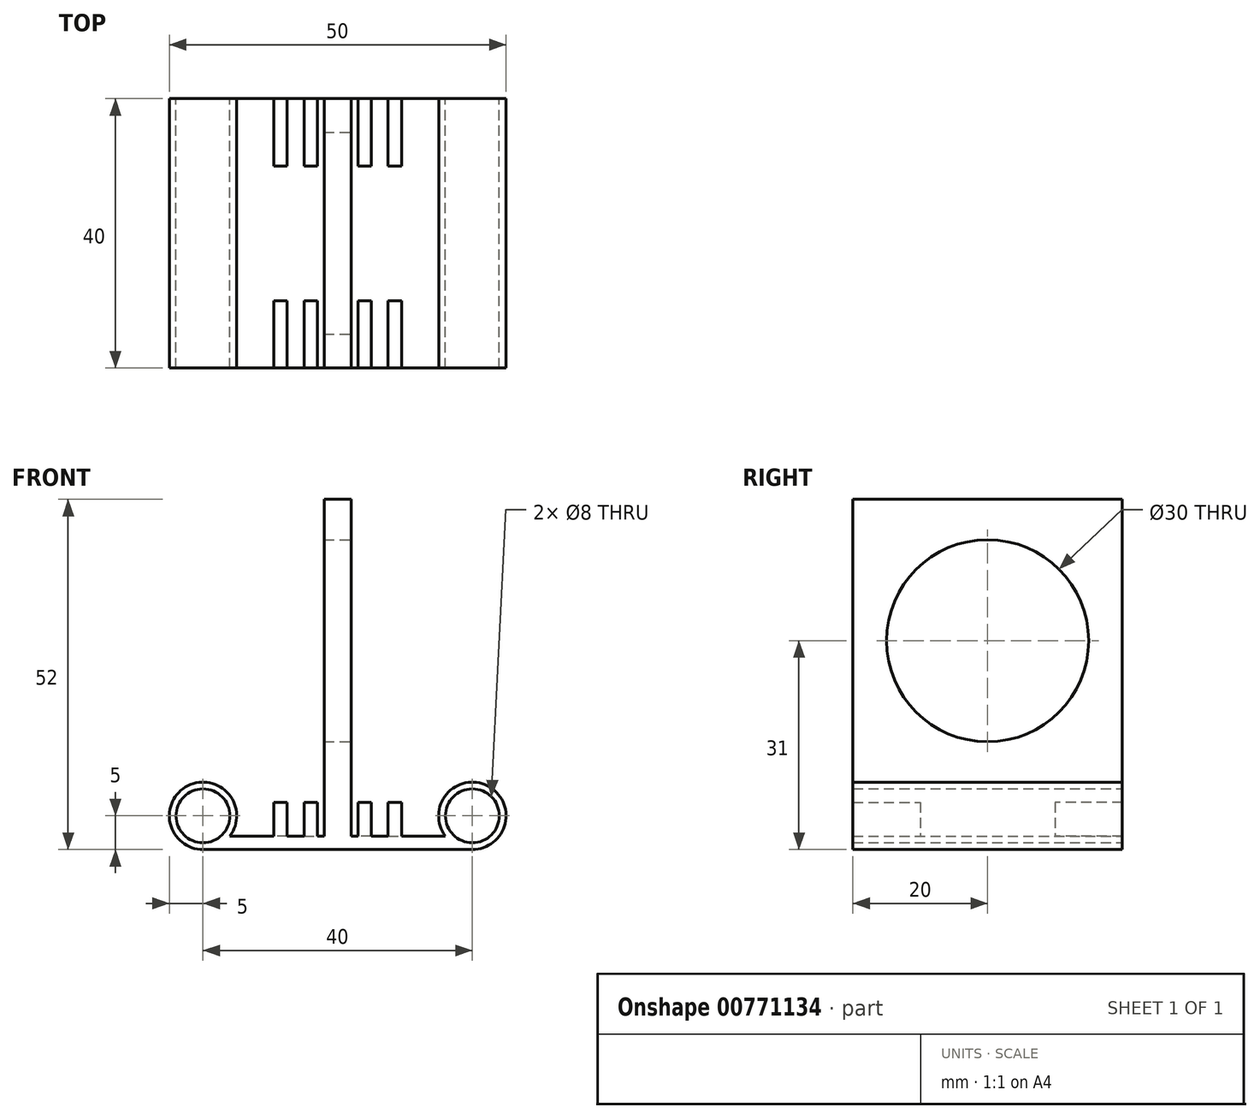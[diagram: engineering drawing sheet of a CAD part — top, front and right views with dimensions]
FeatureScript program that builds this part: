
annotation { "Feature Type Name" : "Feature", "Feature Type Description" : "" }
export const myFeature = defineFeature(function(context is Context, id is Id, definition is map)
    precondition{}
    {
        {
            var Q0;
            Q0=qCreatedBy(makeId("Front.planeOp"),FACE);
            var sketch = newSketch(context, id + "F0", { "sketchPlane" : qUnion([Q0])});
            skLineSegment(sketch, "E0.bottom", {"start": v(20, -1) * mm, "end": v(-20, -1) * mm});
            skLineSegment(sketch, "E0.top", {"start": v(16, 1) * mm, "end": v(-20, 1) * mm});
            skLineSegment(sketch, "E0.right", {"start": v(-20, -1) * mm, "end": v(-20, 1) * mm});
            skPoint(sketch, "E0.middle", {"position": v(0, 0) * mm});
            skArc(sketch, "E1", {"start": v(20, -1) * mm, "mid": v(22.24, 8.47) * mm, "end": v(16, 1) * mm});
            skPoint(sketch, "E1.second.point", {"position": v(20, 9) * mm});
            skPoint(sketch, "E1.third.point", {"position": v(24.89, 5.05) * mm});
            skCircle(sketch, "E2", {"center": v(20, 4) * mm, "radius": 4 * mm});
            skPoint(sketch, "E3.orphan", {"position": v(20, 1) * mm});
            skLineSegment(sketch, "E4.bottom", {"start": v(-2, 1) * mm, "end": v(2, 1) * mm});
            skLineSegment(sketch, "E4.top", {"start": v(-2, 51) * mm, "end": v(2, 51) * mm});
            skLineSegment(sketch, "E4.left", {"start": v(-2, 1) * mm, "end": v(-2, 51) * mm});
            skLineSegment(sketch, "E4.right", {"start": v(2, 1) * mm, "end": v(2, 51) * mm});
            skArc(sketch, "E5.MirrorCS", {"start": v(-20, -1) * mm, "mid": v(-22.24, 8.47) * mm, "end": v(-16, 1) * mm});
            skCircle(sketch, "E6.MirrorC", {"center": v(-20, 4) * mm, "radius": 4 * mm});
            skPoint(sketch, "E7.MirrorP", {"position": v(-20, 9) * mm});
            skPoint(sketch, "E8.MirrorP", {"position": v(-24.89, 5.05) * mm});
            skPoint(sketch, "E9.MirrorP", {"position": v(-20, 1) * mm});
            skSolve(sketch);
        }
        {
            var Q0;
            Q0 = qSketchRegion(id + "F0", true);
            extrude(context, id + "F1", {"entities" : qUnion([Q0]), "endBound" : BoundingType.SYMMETRIC, "depth" : 40 * mm, "offsetDistance" : 25 * mm});
        }
        {
            var Q0;
            {var subQ0=sQuery(id+"F0.wireOp",EDGE,"E0.top");Q0=makeQuery(id+"F1.opExtrude","SWEPT_FACE",FACE,{"disambiguationData":[OSD([subQ0]),TDD([makeQuery(id+"F0.imprint","IMPRINT",EDGE,{"disambiguationData":[TD([[makeQuery(id+"F0.imprint","INTERSECT",VERTEX,{"derivedFrom":[subQ0,sQuery(id+"F0.wireOp",EDGE,"E1")]}),-1.0]])],"derivedFrom":subQ0})])]});}
            var sketch = newSketch(context, id + "F2", { "sketchPlane" : qUnion([Q0])});
            skLineSegment(sketch, "E10.bottom", {"start": v(7.5, -20) * mm, "end": v(9.5, -20) * mm});
            skLineSegment(sketch, "E10.top", {"start": v(7.5, -10) * mm, "end": v(9.5, -10) * mm});
            skLineSegment(sketch, "E10.left", {"start": v(7.5, -20) * mm, "end": v(7.5, -10) * mm});
            skLineSegment(sketch, "E10.right", {"start": v(9.5, -20) * mm, "end": v(9.5, -10) * mm});
            skLineSegment(sketch, "E11.bottom", {"start": v(5, -20) * mm, "end": v(3, -20) * mm});
            skLineSegment(sketch, "E11.top", {"start": v(5, -10) * mm, "end": v(3, -10) * mm});
            skLineSegment(sketch, "E11.left", {"start": v(5, -20) * mm, "end": v(5, -10) * mm});
            skLineSegment(sketch, "E11.right", {"start": v(3, -20) * mm, "end": v(3, -10) * mm});
            skLineSegment(sketch, "E12.MirrorCS", {"start": v(-7.5, -20) * mm, "end": v(-7.5, -10) * mm});
            skLineSegment(sketch, "E13.MirrorCS", {"start": v(-5, -20) * mm, "end": v(-3, -20) * mm});
            skLineSegment(sketch, "E14.MirrorCS", {"start": v(-5, -20) * mm, "end": v(-5, -10) * mm});
            skLineSegment(sketch, "E15.MirrorCS", {"start": v(-3, -20) * mm, "end": v(-3, -10) * mm});
            skLineSegment(sketch, "E16.MirrorCS", {"start": v(-7.5, -20) * mm, "end": v(-9.5, -20) * mm});
            skLineSegment(sketch, "E17.MirrorCS", {"start": v(-9.5, -20) * mm, "end": v(-9.5, -10) * mm});
            skLineSegment(sketch, "E18.MirrorCS", {"start": v(-5, -10) * mm, "end": v(-3, -10) * mm});
            skLineSegment(sketch, "E19.MirrorCS", {"start": v(-7.5, -10) * mm, "end": v(-9.5, -10) * mm});
            skLineSegment(sketch, "E20.MirrorCS", {"start": v(7.5, 10) * mm, "end": v(9.5, 10) * mm});
            skLineSegment(sketch, "E21.MirrorCS", {"start": v(-7.5, 10) * mm, "end": v(-9.5, 10) * mm});
            skLineSegment(sketch, "E22.MirrorCS", {"start": v(7.5, 20) * mm, "end": v(9.5, 20) * mm});
            skLineSegment(sketch, "E23.MirrorCS", {"start": v(-5, 10) * mm, "end": v(-3, 10) * mm});
            skLineSegment(sketch, "E24.MirrorCS", {"start": v(5, 20) * mm, "end": v(3, 20) * mm});
            skLineSegment(sketch, "E25.MirrorCS", {"start": v(-7.5, 20) * mm, "end": v(-9.5, 20) * mm});
            skLineSegment(sketch, "E26.MirrorCS", {"start": v(-5, 20) * mm, "end": v(-3, 20) * mm});
            skLineSegment(sketch, "E27.MirrorCS", {"start": v(5, 10) * mm, "end": v(3, 10) * mm});
            skLineSegment(sketch, "E28.MirrorCS", {"start": v(-7.5, 20) * mm, "end": v(-7.5, 10) * mm});
            skLineSegment(sketch, "E29.MirrorCS", {"start": v(3, 20) * mm, "end": v(3, 10) * mm});
            skLineSegment(sketch, "E30.MirrorCS", {"start": v(-9.5, 20) * mm, "end": v(-9.5, 10) * mm});
            skLineSegment(sketch, "E31.MirrorCS", {"start": v(5, 20) * mm, "end": v(5, 10) * mm});
            skLineSegment(sketch, "E32.MirrorCS", {"start": v(9.5, 20) * mm, "end": v(9.5, 10) * mm});
            skLineSegment(sketch, "E33.MirrorCS", {"start": v(-3, 20) * mm, "end": v(-3, 10) * mm});
            skLineSegment(sketch, "E34.MirrorCS", {"start": v(-5, 20) * mm, "end": v(-5, 10) * mm});
            skLineSegment(sketch, "E35.MirrorCS", {"start": v(7.5, 20) * mm, "end": v(7.5, 10) * mm});
            skSolve(sketch);
        }
        {
            var Q0;
            Q0 = qSketchRegion(id + "F2", true);
            extrude(context, id + "F3", {"entities" : qUnion([Q0]), "operationType" : NewBodyOperationType.ADD, "depth" : 5 * mm, "offsetDistance" : 25 * mm});
        }
        {
            var Q0;
            Q0=makeQuery(id+"F1.opExtrude","SWEPT_FACE",FACE,{"disambiguationData":[OSD([sQuery(id+"F0.wireOp",EDGE,"E4.right")])]});
            var sketch = newSketch(context, id + "F4", { "sketchPlane" : qUnion([Q0])});
            skCircle(sketch, "E36", {"center": v(0, 30) * mm, "radius": 15 * mm});
            skSolve(sketch);
        }
        {
            var Q0;
            Q0 = qSketchRegion(id + "F4", true);
            extrude(context, id + "F5", {"entities" : qUnion([Q0]), "operationType" : NewBodyOperationType.REMOVE, "oppositeDirection" : true, "depth" : 25 * mm, "offsetDistance" : 25 * mm});
        }
        {
            var Q0;
            Q0 = qSketchRegion(id + "F2", true);
            extrude(context, id + "F6", {"entities" : qUnion([Q0]), "operationType" : NewBodyOperationType.ADD, "depth" : 5 * mm, "offsetDistance" : 25 * mm});
        }
    });
